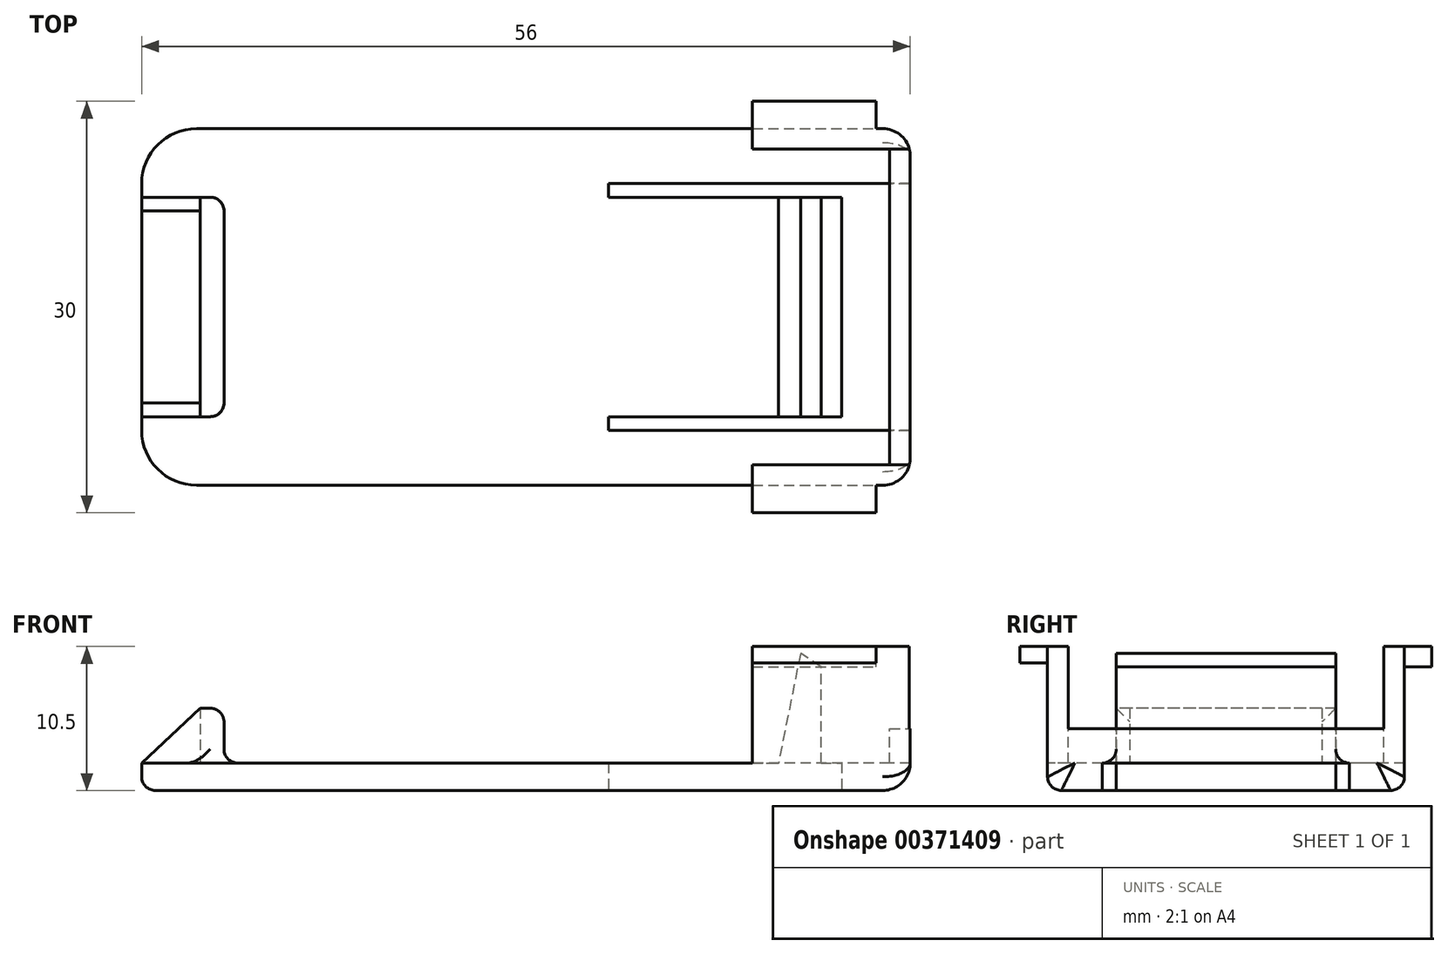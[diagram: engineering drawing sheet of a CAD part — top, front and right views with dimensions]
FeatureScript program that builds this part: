
annotation { "Feature Type Name" : "Feature", "Feature Type Description" : "" }
export const myFeature = defineFeature(function(context is Context, id is Id, definition is map)
    precondition{}
    {
        {
            var Q0;
            Q0=qCreatedBy(makeId("Top.planeOp"),FACE);
            var sketch = newSketch(context, id + "F0", { "sketchPlane" : qUnion([Q0])});
            skLineSegment(sketch, "E0.bottom", {"start": v(28, 13) * mm, "end": v(-24, 13) * mm});
            skLineSegment(sketch, "E0.top", {"start": v(28, -13) * mm, "end": v(-24, -13) * mm});
            skLineSegment(sketch, "E0.left", {"start": v(28, 13) * mm, "end": v(28, 9) * mm});
            skLineSegment(sketch, "E0.right", {"start": v(-28, 9) * mm, "end": v(-28, -9) * mm});
            skPoint(sketch, "E0.middle", {"position": v(0, 0) * mm});
            skLineSegment(sketch, "E1.bottom", {"start": v(28, 9) * mm, "end": v(6, 9) * mm});
            skLineSegment(sketch, "E1.top", {"start": v(28, -9) * mm, "end": v(6, -9) * mm});
            skLineSegment(sketch, "E1.right", {"start": v(6, 9) * mm, "end": v(6, 8) * mm});
            skLineSegment(sketch, "E2.trimOffspring", {"start": v(28, -9) * mm, "end": v(28, -13) * mm});
            skLineSegment(sketch, "E3.bottom", {"start": v(6, 8) * mm, "end": v(23, 8) * mm});
            skLineSegment(sketch, "E3.top", {"start": v(6, -8) * mm, "end": v(23, -8) * mm});
            skLineSegment(sketch, "E3.right", {"start": v(23, 8) * mm, "end": v(23, -8) * mm});
            skLineSegment(sketch, "E4.trimOffspring", {"start": v(6, -8) * mm, "end": v(6, -9) * mm});
            skPoint(sketch, "E5.visualSharp", {"position": v(-28, 13) * mm});
            skArc(sketch, "E5.filletArc", {"start": v(-24, 13) * mm, "mid": v(-26.83, 11.83) * mm, "end": v(-28, 9) * mm});
            skPoint(sketch, "E6.visualSharp", {"position": v(-28, -13) * mm});
            skArc(sketch, "E6.filletArc", {"start": v(-28, -9) * mm, "mid": v(-26.83, -11.83) * mm, "end": v(-24, -13) * mm});
            skSolve(sketch);
        }
        {
            var Q0;
            Q0=makeQuery(id+"F0.imprint","IMPRINT",FACE,{"disambiguationData":[TD([[makeQuery(id+"F0.imprint","IMPRINT",EDGE,{"derivedFrom":sQuery(id+"F0.wireOp",EDGE,"E0.bottom")}),1.0]])]});
            extrude(context, id + "F1", {"entities" : qUnion([Q0]), "depth" : 2 * mm});
        }
        {
            var Q0;
            Q0=makeQuery(id+"F1.opExtrude","CAP_FACE",FACE,{"disambiguationData":[OSD([sQuery(id+"F0.wireOp",EDGE,"E0.bottom"),sQuery(id+"F0.wireOp",EDGE,"E0.top"),sQuery(id+"F0.wireOp",EDGE,"E0.left"),sQuery(id+"F0.wireOp",EDGE,"E0.right"),sQuery(id+"F0.wireOp",EDGE,"E1.bottom"),sQuery(id+"F0.wireOp",EDGE,"E1.top"),sQuery(id+"F0.wireOp",EDGE,"E1.right"),sQuery(id+"F0.wireOp",EDGE,"E2.trimOffspring"),sQuery(id+"F0.wireOp",EDGE,"E3.bottom"),sQuery(id+"F0.wireOp",EDGE,"E3.top"),sQuery(id+"F0.wireOp",EDGE,"E3.right"),sQuery(id+"F0.wireOp",EDGE,"E4.trimOffspring"),sQuery(id+"F0.wireOp",EDGE,"E5.filletArc"),sQuery(id+"F0.wireOp",EDGE,"E6.filletArc")])],"isStart":false});
            var sketch = newSketch(context, id + "F2", { "sketchPlane" : qUnion([Q0])});
            skLineSegment(sketch, "E7.bottom", {"start": v(-23.75, 8) * mm, "end": v(-22, 8) * mm});
            skLineSegment(sketch, "E7.top", {"start": v(-23.75, -8) * mm, "end": v(-22, -8) * mm});
            skLineSegment(sketch, "E7.left", {"start": v(-23.75, 8) * mm, "end": v(-23.75, -8) * mm});
            skLineSegment(sketch, "E7.right", {"start": v(-22, 8) * mm, "end": v(-22, -8) * mm});
            skSolve(sketch);
        }
        {
            var Q0;
            Q0=makeQuery(id+"F2.imprint","IMPRINT",FACE,{"disambiguationData":[TD([[makeQuery(id+"F2.imprint","IMPRINT",EDGE,{"derivedFrom":sQuery(id+"F2.wireOp",EDGE,"E7.bottom")}),-1.0]])]});
            extrude(context, id + "F3", {"entities" : qUnion([Q0]), "operationType" : NewBodyOperationType.ADD, "depth" : 4 * mm});
        }
        {
            var Q0;
            Q0=makeQuery(id+"F3.opExtrude","SWEPT_FACE",FACE,{"disambiguationData":[OSD([sQuery(id+"F2.wireOp",EDGE,"E7.top")])]});
            var sketch = newSketch(context, id + "F4", { "sketchPlane" : qUnion([Q0])});
            skLineSegment(sketch, "E8", {"start": v(-23.75, 6) * mm, "end": v(-27.98, 2) * mm});
            skLineSegment(sketch, "E9", {"start": v(-27.98, 2) * mm, "end": v(-23.75, 2) * mm});
            skLineSegment(sketch, "E10", {"start": v(-23.75, 2) * mm, "end": v(-23.75, 6) * mm});
            skSolve(sketch);
        }
        {
            var Q0;
            Q0=makeQuery(id+"F4.imprint","IMPRINT",FACE,{"disambiguationData":[TD([[makeQuery(id+"F4.imprint","IMPRINT",EDGE,{"derivedFrom":sQuery(id+"F4.wireOp",EDGE,"E8")}),1.0]])]});
            extrude(context, id + "F5", {"entities" : qUnion([Q0]), "operationType" : NewBodyOperationType.ADD, "oppositeDirection" : true, "depth" : 1 * mm});
        }
        {
            var Q0;
            Q0=makeQuery(id+"F3.opExtrude","SWEPT_FACE",FACE,{"disambiguationData":[OSD([sQuery(id+"F2.wireOp",EDGE,"E7.bottom")])]});
            var sketch = newSketch(context, id + "F6", { "sketchPlane" : qUnion([Q0])});
            skLineSegment(sketch, "E11", {"start": v(23.75, 2) * mm, "end": v(23.75, 6) * mm});
            skLineSegment(sketch, "E12.MirrorCS", {"start": v(28, 2) * mm, "end": v(23.75, 2) * mm});
            skLineSegment(sketch, "E13.MirrorCS", {"start": v(23.75, 6) * mm, "end": v(28, 2) * mm});
            skSolve(sketch);
        }
        {
            var Q0;
            {var subQ6=sQuery(id+"F6.wireOp",EDGE,"E13.MirrorCS");Q0=makeQuery(id+"F6.imprint","IMPRINT",FACE,{"disambiguationData":[TD([[makeQuery(id+"F6.imprint","IMPRINT",EDGE,{"derivedFrom":subQ6}),-1.0]])]});}
            extrude(context, id + "F7", {"entities" : qUnion([Q0]), "operationType" : NewBodyOperationType.ADD, "oppositeDirection" : true, "depth" : 1 * mm});
        }
        {
            var Q0;
            Q0=makeQuery(id+"F1.opExtrude","SWEPT_FACE",FACE,{"disambiguationData":[OSD([sQuery(id+"F0.wireOp",EDGE,"E3.top")])]});
            var sketch = newSketch(context, id + "F8", { "sketchPlane" : qUnion([Q0])});
            skLineSegment(sketch, "E14", {"start": v(21.5, 2) * mm, "end": v(21.5, 9) * mm});
            skLineSegment(sketch, "E15", {"start": v(21.5, 9) * mm, "end": v(20, 10) * mm});
            skLineSegment(sketch, "E16", {"start": v(20, 10) * mm, "end": v(18.4, 2) * mm});
            skLineSegment(sketch, "E17", {"start": v(18.4, 2) * mm, "end": v(21.5, 2) * mm});
            skSolve(sketch);
        }
        {
            var Q0;
            Q0=makeQuery(id+"F1.opExtrude","SWEPT_FACE",FACE,{"disambiguationData":[OSD([sQuery(id+"F0.wireOp",EDGE,"E0.top")])]});
            var sketch = newSketch(context, id + "F9", { "sketchPlane" : qUnion([Q0])});
            skLineSegment(sketch, "E18.bottom", {"start": v(16.5, 2) * mm, "end": v(28, 2) * mm});
            skLineSegment(sketch, "E18.top", {"start": v(16.5, 10.5) * mm, "end": v(28, 10.5) * mm});
            skLineSegment(sketch, "E18.left", {"start": v(16.5, 2) * mm, "end": v(16.5, 10.5) * mm});
            skLineSegment(sketch, "E18.right", {"start": v(28, 2) * mm, "end": v(28, 10.5) * mm});
            skSolve(sketch);
        }
        {
            var Q0;
            Q0=makeQuery(id+"F9.imprint","IMPRINT",FACE,{"disambiguationData":[TD([[makeQuery(id+"F9.imprint","IMPRINT",EDGE,{"derivedFrom":sQuery(id+"F9.wireOp",EDGE,"E18.bottom")}),-1.0]])]});
            extrude(context, id + "F10", {"entities" : qUnion([Q0]), "operationType" : NewBodyOperationType.ADD, "oppositeDirection" : true, "depth" : 26 * mm});
        }
        {
            var Q0;
            Q0=makeQuery(id+"F10.opExtrude","SWEPT_FACE",FACE,{"disambiguationData":[OSD([sQuery(id+"F9.wireOp",EDGE,"E18.top")])]});
            var sketch = newSketch(context, id + "F11", { "sketchPlane" : qUnion([Q0])});
            skLineSegment(sketch, "E19.bottom", {"start": v(28, -11.5) * mm, "end": v(16.5, -11.5) * mm});
            skLineSegment(sketch, "E19.top", {"start": v(28, 11.5) * mm, "end": v(16.5, 11.5) * mm});
            skLineSegment(sketch, "E19.left", {"start": v(28, -11.5) * mm, "end": v(28, 11.5) * mm});
            skLineSegment(sketch, "E19.right", {"start": v(16.5, -11.5) * mm, "end": v(16.5, 11.5) * mm});
            skSolve(sketch);
        }
        {
            var Q0;
            Q0 = qSketchRegion(id + "F11", true);
            extrude(context, id + "F12", {"entities" : qUnion([Q0]), "operationType" : NewBodyOperationType.REMOVE, "oppositeDirection" : true, "offsetDistance" : 25 * mm, "depth" : 8.5 * mm});
        }
        {
            var Q0;
            Q0=makeQuery(id+"F8.imprint","IMPRINT",FACE,{"disambiguationData":[TD([[makeQuery(id+"F8.imprint","IMPRINT",EDGE,{"derivedFrom":sQuery(id+"F8.wireOp",EDGE,"E14")}),1.0]])]});
            extrude(context, id + "F13", {"entities" : qUnion([Q0]), "operationType" : NewBodyOperationType.ADD, "oppositeDirection" : true, "depth" : 16 * mm});
        }
        {
            var Q0;
            {var subQ0=sQuery(id+"F0.wireOp",EDGE,"E0.top");var subQ2=sQuery(id+"F9.wireOp",EDGE,"E18.right");var subQ10=sQuery(id+"F0.wireOp",EDGE,"E2.trimOffspring");var subQ14=sQuery(id+"F0.wireOp",EDGE,"E0.left");Q0=makeQuery(id+"F12.boolean.opBoolean","SPLIT",FACE,{"disambiguationData":[TD([makeQuery(id+"F1.opExtrude","SWEPT_FACE",FACE,{"disambiguationData":[OSD([subQ0])]})])],"derivedFrom":makeQuery(id+"F10.boolean.opBoolean","MERGE",FACE,{"derivedFrom":[makeQuery(id+"F1.opExtrude","SWEPT_FACE",FACE,{"disambiguationData":[OSD([subQ14])]}),makeQuery(id+"F1.opExtrude","SWEPT_FACE",FACE,{"disambiguationData":[OSD([subQ10])]}),makeQuery(id+"F10.opExtrude","SWEPT_FACE",FACE,{"disambiguationData":[OSD([subQ2])]})]})});}
            var sketch = newSketch(context, id + "F14", { "sketchPlane" : qUnion([Q0])});
            skLineSegment(sketch, "E20.bottom", {"start": v(-11.5, 2) * mm, "end": v(11.5, 2) * mm});
            skLineSegment(sketch, "E20.top", {"start": v(-11.5, 4.5) * mm, "end": v(-10, 4.5) * mm});
            skLineSegment(sketch, "E20.left", {"start": v(-11.5, 2) * mm, "end": v(-11.5, 4.5) * mm});
            skLineSegment(sketch, "E20.right", {"start": v(11.5, 2) * mm, "end": v(11.5, 4.5) * mm});
            skLineSegment(sketch, "E21.top", {"start": v(-10, 7.5) * mm, "end": v(-9, 7.5) * mm});
            skLineSegment(sketch, "E21.left", {"start": v(-10, 4.5) * mm, "end": v(-10, 7.5) * mm});
            skLineSegment(sketch, "E21.right", {"start": v(-9, 4.5) * mm, "end": v(-9, 7.5) * mm});
            skLineSegment(sketch, "E22.top", {"start": v(9, 7.5) * mm, "end": v(10, 7.5) * mm});
            skLineSegment(sketch, "E22.left", {"start": v(9, 4.5) * mm, "end": v(9, 7.5) * mm});
            skLineSegment(sketch, "E22.right", {"start": v(10, 4.5) * mm, "end": v(10, 7.5) * mm});
            skLineSegment(sketch, "E23.trimOffspring", {"start": v(-9, 4.5) * mm, "end": v(9, 4.5) * mm});
            skLineSegment(sketch, "E24.trimOffspring", {"start": v(10, 4.5) * mm, "end": v(11.5, 4.5) * mm});
            skLineSegment(sketch, "E25", {"start": v(-10, 4.5) * mm, "end": v(-9, 4.5) * mm});
            skLineSegment(sketch, "E26", {"start": v(9, 4.5) * mm, "end": v(10, 4.5) * mm});
            skSolve(sketch);
        }
        {
            var Q0;
            Q0=makeQuery(id+"F14.imprint","IMPRINT",FACE,{"disambiguationData":[TD([[makeQuery(id+"F14.imprint","IMPRINT",EDGE,{"derivedFrom":sQuery(id+"F14.wireOp",EDGE,"E20.top")}),-1.0]])]});
            extrude(context, id + "F15", {"entities" : qUnion([Q0]), "operationType" : NewBodyOperationType.ADD, "oppositeDirection" : true, "depth" : 1.5 * mm});
        }
        {
            var Q0;
            {var subQ2=sQuery(id+"F9.wireOp",EDGE,"E18.top");Q0=makeQuery(id+"F12.boolean.opBoolean","SPLIT",FACE,{"disambiguationData":[TD([makeQuery(id+"F1.opExtrude","SWEPT_FACE",FACE,{"disambiguationData":[OSD([sQuery(id+"F0.wireOp",EDGE,"E0.top")])]})])],"derivedFrom":makeQuery(id+"F10.opExtrude","SWEPT_FACE",FACE,{"disambiguationData":[OSD([subQ2])]})});}
            var sketch = newSketch(context, id + "F16", { "sketchPlane" : qUnion([Q0])});
            skLineSegment(sketch, "E27.bottom", {"start": v(16.5, -11.5) * mm, "end": v(25.5, -11.5) * mm});
            skLineSegment(sketch, "E27.top", {"start": v(16.5, -15) * mm, "end": v(25.5, -15) * mm});
            skLineSegment(sketch, "E27.left", {"start": v(16.5, -11.5) * mm, "end": v(16.5, -15) * mm});
            skLineSegment(sketch, "E27.right", {"start": v(25.5, -11.5) * mm, "end": v(25.5, -15) * mm});
            skSolve(sketch);
        }
        {
            var Q0;
            {var subQ0=sQuery(id+"F16.wireOp",EDGE,"E27.top");Q0=makeQuery(id+"F16.imprint","IMPRINT",FACE,{"disambiguationData":[TD([[makeQuery(id+"F16.imprint","IMPRINT",EDGE,{"derivedFrom":subQ0}),1.0]])]});}
            extrude(context, id + "F17", {"entities" : qUnion([Q0]), "operationType" : NewBodyOperationType.ADD, "oppositeDirection" : true, "depth" : 1.2 * mm});
        }
        {
            var Q0;
            {var subQ2=sQuery(id+"F9.wireOp",EDGE,"E18.top");Q0=makeQuery(id+"F12.boolean.opBoolean","SPLIT",FACE,{"disambiguationData":[TD([makeQuery(id+"F1.opExtrude","SWEPT_FACE",FACE,{"disambiguationData":[OSD([sQuery(id+"F0.wireOp",EDGE,"E0.bottom")])]})])],"derivedFrom":makeQuery(id+"F10.opExtrude","SWEPT_FACE",FACE,{"disambiguationData":[OSD([subQ2])]})});}
            var sketch = newSketch(context, id + "F18", { "sketchPlane" : qUnion([Q0])});
            skLineSegment(sketch, "E28.bottom", {"start": v(16.5, 11.5) * mm, "end": v(25.5, 11.5) * mm});
            skLineSegment(sketch, "E28.top", {"start": v(16.5, 15) * mm, "end": v(25.5, 15) * mm});
            skLineSegment(sketch, "E28.left", {"start": v(16.5, 11.5) * mm, "end": v(16.5, 15) * mm});
            skLineSegment(sketch, "E28.right", {"start": v(25.5, 11.5) * mm, "end": v(25.5, 15) * mm});
            skSolve(sketch);
        }
        {
            var Q0;
            {var subQ0=sQuery(id+"F18.wireOp",EDGE,"E28.top");Q0=makeQuery(id+"F18.imprint","IMPRINT",FACE,{"disambiguationData":[TD([[makeQuery(id+"F18.imprint","IMPRINT",EDGE,{"derivedFrom":subQ0}),-1.0]])]});}
            extrude(context, id + "F19", {"entities" : qUnion([Q0]), "operationType" : NewBodyOperationType.ADD, "oppositeDirection" : true, "depth" : 1.5 * mm});
        }
        {
            var Q0;
            Q0=makeQuery(id+"F1.opExtrude","CAP_EDGE",EDGE,{"disambiguationData":[OSD([sQuery(id+"F0.wireOp",EDGE,"E0.right")])],"isStart":true});
            fillet(context, id + "F20", {"entities" : qUnion([Q0]), "radius" : 1 * mm, "tangentPropagation" : true, "allowEdgeOverflow" : false});
        }
        {
            var Q0;
            Q0=makeQuery(id+"F1.opExtrude","CAP_EDGE",EDGE,{"disambiguationData":[OSD([sQuery(id+"F0.wireOp",EDGE,"E2.trimOffspring")])],"isStart":true});
            var Q1;
            Q1=makeQuery(id+"F1.opExtrude","CAP_EDGE",EDGE,{"disambiguationData":[OSD([sQuery(id+"F0.wireOp",EDGE,"E0.left")])],"isStart":true});
            fillet(context, id + "F21", {"entities" : qUnion([Q0, Q1]), "radius" : 2 * mm, "tangentPropagation" : true, "allowEdgeOverflow" : false});
        }
        {
            var Q0;
            Q0=makeQuery(id+"F3.opExtrude","SWEPT_FACE",FACE,{"disambiguationData":[OSD([sQuery(id+"F2.wireOp",EDGE,"E7.right")])]});
            fillet(context, id + "F22", {"entities" : qUnion([Q0]), "radius" : 1 * mm, "tangentPropagation" : true, "allowEdgeOverflow" : false});
        }
    });
